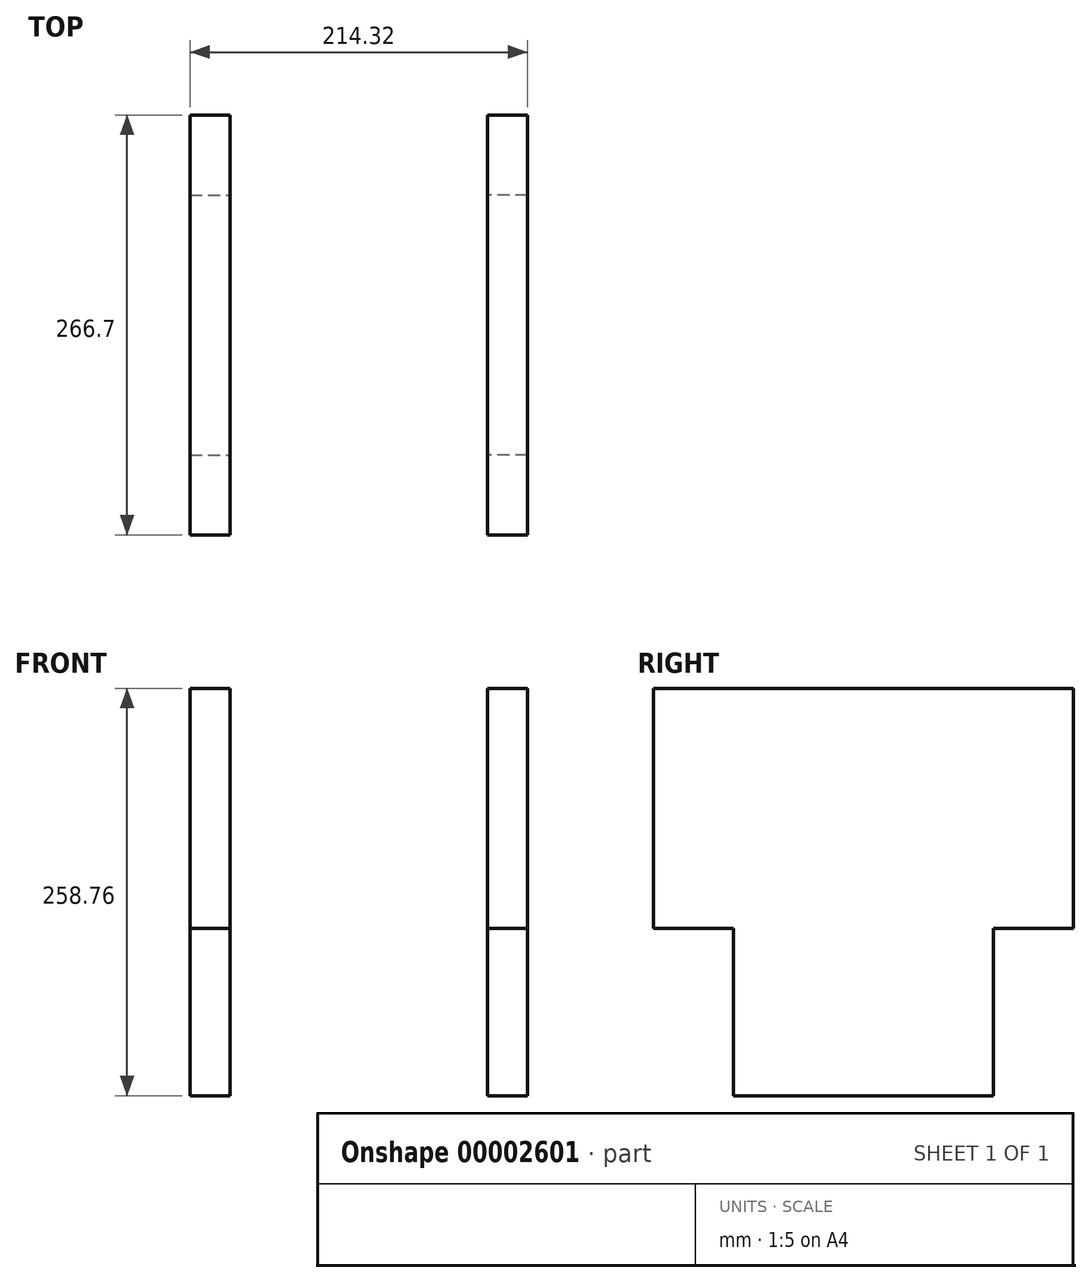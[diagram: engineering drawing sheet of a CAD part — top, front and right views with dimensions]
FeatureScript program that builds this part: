
annotation { "Feature Type Name" : "Feature", "Feature Type Description" : "" }
export const myFeature = defineFeature(function(context is Context, id is Id, definition is map)
    precondition{}
    {
        {
            var Q0;
            Q0=qCreatedBy(makeId("Top.planeOp"),FACE);
            var sketch = newSketch(context, id + "F0", { "sketchPlane" : qUnion([Q0])});
            skLineSegment(sketch, "E0.bottom", {"start": v(-107.16, 82.55) * mm, "end": v(-81.76, 82.55) * mm});
            skLineSegment(sketch, "E0.top", {"start": v(-107.16, -82.55) * mm, "end": v(-81.76, -82.55) * mm});
            skLineSegment(sketch, "E0.left", {"start": v(-107.16, 82.55) * mm, "end": v(-107.16, -82.55) * mm});
            skLineSegment(sketch, "E0.right", {"start": v(-81.76, 82.55) * mm, "end": v(-81.76, -82.55) * mm});
            skLineSegment(sketch, "E1.0.MirrorCS", {"start": v(81.76, 82.55) * mm, "end": v(81.76, -82.55) * mm});
            skLineSegment(sketch, "E2.0.MirrorCS", {"start": v(107.16, 82.55) * mm, "end": v(81.76, 82.55) * mm});
            skLineSegment(sketch, "E3.0.MirrorCS", {"start": v(107.16, 82.55) * mm, "end": v(107.16, -82.55) * mm});
            skLineSegment(sketch, "E4.0.MirrorCS", {"start": v(107.16, -82.55) * mm, "end": v(81.76, -82.55) * mm});
            skSolve(sketch);
        }
        {
            var Q0;
            Q0 = qSketchRegion(id + "F0", true);
            extrude(context, id + "F1", {"entities" : qUnion([Q0]), "depth" : 106.36 * mm});
        }
        {
            var Q0;
            Q0=makeQuery(id+"F1.opExtrude","CAP_FACE",FACE,{"disambiguationData":[OSD([sQuery(id+"F0.wireOp",EDGE,"E0.bottom"),sQuery(id+"F0.wireOp",EDGE,"E0.top"),sQuery(id+"F0.wireOp",EDGE,"E0.left"),sQuery(id+"F0.wireOp",EDGE,"E0.right")])],"isStart":false});
            var sketch = newSketch(context, id + "F2", { "sketchPlane" : qUnion([Q0])});
            skLineSegment(sketch, "E5.bottom", {"start": v(-107.16, 133.35) * mm, "end": v(-81.76, 133.35) * mm});
            skLineSegment(sketch, "E5.top", {"start": v(-107.16, -133.35) * mm, "end": v(-81.76, -133.35) * mm});
            skLineSegment(sketch, "E5.left", {"start": v(-107.16, 133.35) * mm, "end": v(-107.16, -133.35) * mm});
            skLineSegment(sketch, "E5.right", {"start": v(-81.76, 133.35) * mm, "end": v(-81.76, -133.35) * mm});
            skLineSegment(sketch, "E6.0.MirrorCS", {"start": v(81.76, 133.35) * mm, "end": v(81.76, -133.35) * mm});
            skLineSegment(sketch, "E7.0.MirrorCS", {"start": v(107.16, 133.35) * mm, "end": v(81.76, 133.35) * mm});
            skLineSegment(sketch, "E8.0.MirrorCS", {"start": v(107.16, 133.35) * mm, "end": v(107.16, -133.35) * mm});
            skLineSegment(sketch, "E9.0.MirrorCS", {"start": v(107.16, -133.35) * mm, "end": v(81.76, -133.35) * mm});
            skSolve(sketch);
        }
        {
            var Q0;
            Q0 = qSketchRegion(id + "F2", true);
            extrude(context, id + "F3", {"entities" : qUnion([Q0]), "operationType" : NewBodyOperationType.ADD, "depth" : 152.4 * mm});
        }
    });
